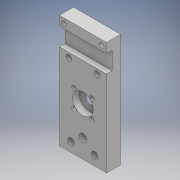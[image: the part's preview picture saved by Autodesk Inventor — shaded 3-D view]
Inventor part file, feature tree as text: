
AUTODESK INVENTOR PART (.ipt)
format: ipt  version: 2018 (Build 220112000, 112)  size: 235,520 bytes
history: native  units: mm
features: sketch x11, extrude x9, projected_geometry x5, hole x2
ambient origin geometry x8: Origin, YZ Plane, XZ Plane, XY Plane, X Axis, Y Axis, Z Axis, Center Point
bodies: Solid1 (feature_tree)
feature tree (27):
  extrude  "Extrusion1"  Depth=120.0mm
  extrude  "Extrusion2"  Depth=15.0mm
  extrude  "Extrusion3"  Depth=5.0mm
  extrude  "Extrusion4"  Depth=10.0mm
  extrude  "Extrusion5"  Depth=20.0mm TaperAngle=0.0deg
  extrude  "Extrusion7"  Depth=47.5mm
  hole  "Hole1"  [1 undecoded]
  hole  "Hole2"  [1 undecoded]
  extrude  "Extrusion8"  Depth=1.7mm TaperAngle=0.0deg
  extrude  "Extrusion11"  Depth=7.0mm TaperAngle=0.0deg
  extrude  "Extrusion12"  Depth=1.0mm
  sketch  "Sketch1"  dims[d0=50.0mm d1=120.0mm]
  sketch  "Sketch2"  dims[d2=15.0mm d3=0.0mm d4=5.0mm]
  sketch  "Sketch3"  dims[d5=5.0mm d6=5.0mm]
  sketch  "Sketch4"  dims[d7=7.0mm d8=10.0mm]
  projected_geometry  "Projected Loop1"
  sketch  "Sketch5"  dims[d9=12.5mm d10=20.0mm d11=0.0mm]
  sketch  "Sketch7"  dims[d12=45.0mm d13=47.5mm]
  sketch  "Sketch8"  dims[d14=5.5mm d15=0.0mm d16=19.0mm]
  sketch  "Sketch10"  dims[d17=6.3mm d18=1.7mm d19=0.0mm]
  sketch  "Sketch11"  dims[d20=9.0mm d21=1.7mm d22=0.0mm]
  projected_geometry  "Projected Loop2"
  projected_geometry  "Projected Loop3"
  projected_geometry  "Projected Loop4"
  sketch  "Sketch14"  dims[d35=22.0mm d36=7.0mm d37=0.0mm]
  sketch  "Sketch15"  dims[d38=45.0deg d39=27.0mm d40=40.0mm d42=360.0deg d44=3.0mm d45=6.0mm d46=5.0mm d47=2.0mm d48=90.0deg d49=8.0mm d50=20.594885mm d53=29.8mm d54=10.0mm d55=5.0mm d56=10.0mm d57=6.0mm d58=6.0mm d59=15.0mm d60=8.0mm d61=19.198622mm d62=8.0mm d63=20.594885mm d69=7.0mm d70=0.0mm d79=8.0mm d80=10.0mm d81=10.0mm d82=0.0mm d83=5.0mm d84=8.0mm d85=0.0mm d88=5.0mm d89=5.0mm d90=1.0mm]
  projected_geometry  "Projected Loop5"
note: 2 required parameter values undecoded (feature->parameter linkage not recoverable at this tier; creation-order binding heuristic only, values carry confidence <= 0.55)
